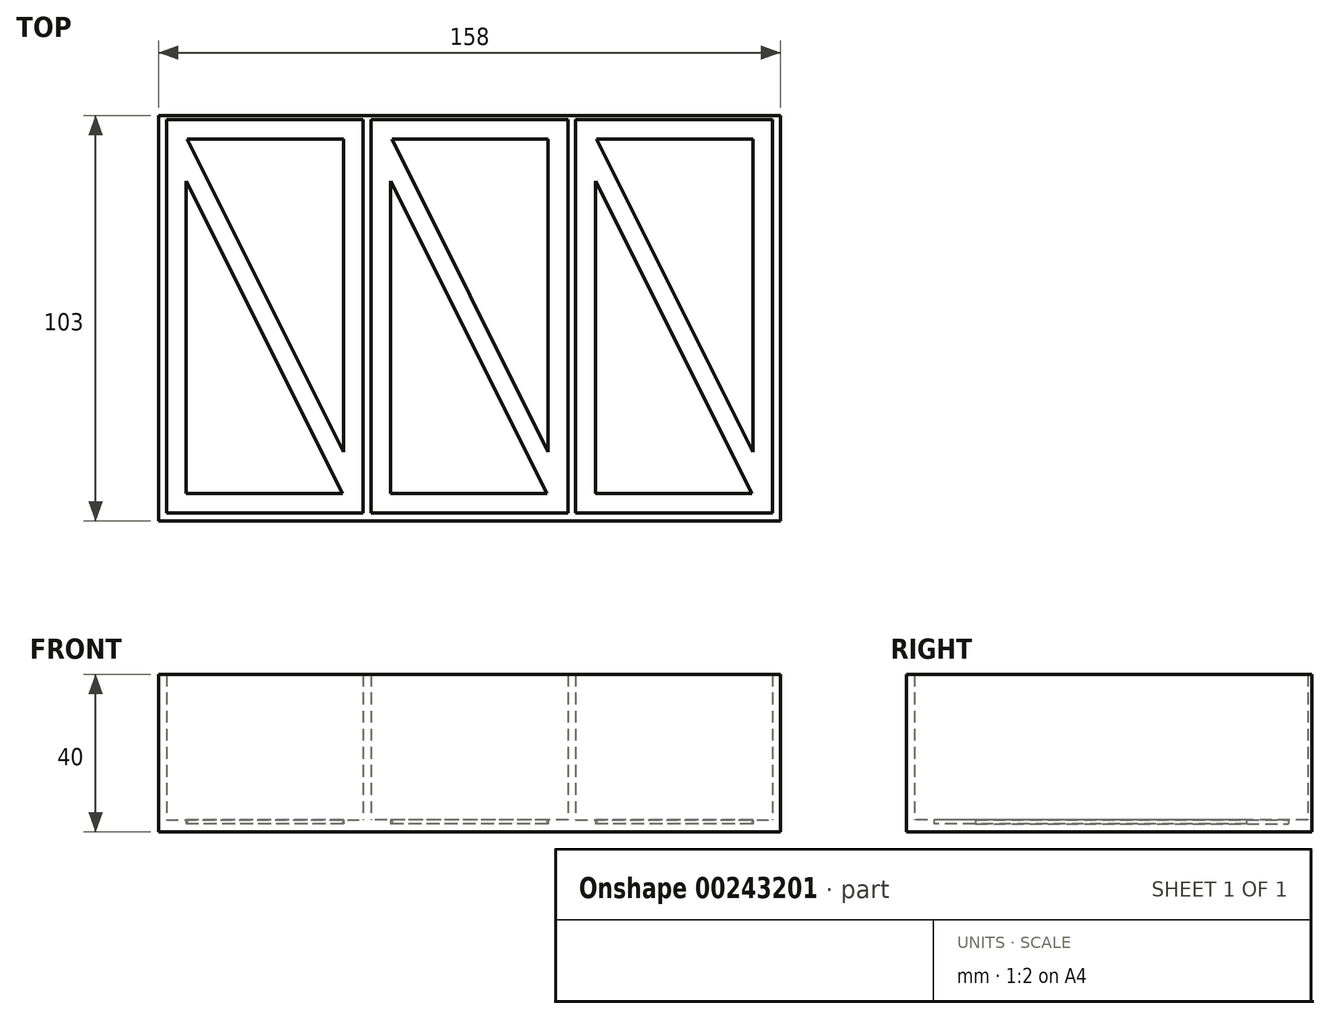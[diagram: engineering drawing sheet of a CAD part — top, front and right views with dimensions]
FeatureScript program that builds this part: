
annotation { "Feature Type Name" : "Feature", "Feature Type Description" : "" }
export const myFeature = defineFeature(function(context is Context, id is Id, definition is map)
    precondition{}
    {
        {
            var Q0;
            Q0=qCreatedBy(makeId("Top.planeOp"),FACE);
            var sketch = newSketch(context, id + "F0", { "sketchPlane" : qUnion([Q0])});
            skLineSegment(sketch, "E0.bottom", {"start": v(-25, 50) * mm, "end": v(25, 50) * mm});
            skLineSegment(sketch, "E0.top", {"start": v(-25, -50) * mm, "end": v(25, -50) * mm});
            skLineSegment(sketch, "E0.left", {"start": v(-25, 50) * mm, "end": v(-25, -50) * mm});
            skLineSegment(sketch, "E0.right", {"start": v(25, 50) * mm, "end": v(25, -50) * mm});
            skLineSegment(sketch, "E1", {"start": v(26, 57.33) * mm, "end": v(26, -203.87) * mm, "construction": true});
            skLineSegment(sketch, "E2.MirrorCS", {"start": v(25, 50) * mm, "end": v(25, 150) * mm});
            skLineSegment(sketch, "E3.MirrorCS", {"start": v(-25, 50) * mm, "end": v(-25, 150) * mm});
            skLineSegment(sketch, "E4.MirrorCS", {"start": v(77, -50) * mm, "end": v(27, -50) * mm});
            skLineSegment(sketch, "E5.MirrorCS", {"start": v(77, 50) * mm, "end": v(77, -50) * mm});
            skLineSegment(sketch, "E6.MirrorCS", {"start": v(27, 50) * mm, "end": v(27, -50) * mm});
            skLineSegment(sketch, "E7.MirrorCS", {"start": v(77, 50) * mm, "end": v(27, 50) * mm});
            skLineSegment(sketch, "E8", {"start": v(78, 65.82) * mm, "end": v(78, -195.37) * mm, "construction": true});
            skLineSegment(sketch, "E9.MirrorCS", {"start": v(79, -50) * mm, "end": v(129, -50) * mm});
            skLineSegment(sketch, "E10.MirrorCS", {"start": v(79, 50) * mm, "end": v(79, -50) * mm});
            skLineSegment(sketch, "E11.MirrorCS", {"start": v(79, 50) * mm, "end": v(129, 50) * mm});
            skLineSegment(sketch, "E12.MirrorCS", {"start": v(129, 50) * mm, "end": v(129, -50) * mm});
            skLineSegment(sketch, "E13.bottom", {"start": v(-27, 51) * mm, "end": v(131, 51) * mm});
            skLineSegment(sketch, "E13.top", {"start": v(-27, -52) * mm, "end": v(131, -52) * mm});
            skLineSegment(sketch, "E13.left", {"start": v(-27, 51) * mm, "end": v(-27, -52) * mm});
            skLineSegment(sketch, "E13.right", {"start": v(131, 51) * mm, "end": v(131, -52) * mm});
            skLineSegment(sketch, "E14", {"start": v(-25, 50) * mm, "end": v(25, -50) * mm, "construction": true});
            skLineSegment(sketch, "E15", {"start": v(-20, 34.4) * mm, "end": v(-20, -45) * mm});
            skLineSegment(sketch, "E16", {"start": v(-20, -45) * mm, "end": v(19.7, -45) * mm});
            skLineSegment(sketch, "E17", {"start": v(19.7, -45) * mm, "end": v(-20, 34.4) * mm});
            skLineSegment(sketch, "E18", {"start": v(-19.7, 45) * mm, "end": v(20, 45) * mm});
            skLineSegment(sketch, "E19", {"start": v(20, 45) * mm, "end": v(20, -34.4) * mm});
            skLineSegment(sketch, "E20", {"start": v(20, -34.4) * mm, "end": v(-19.7, 45) * mm});
            skLineSegment(sketch, "E21.1.0.0", {"start": v(32.3, 45) * mm, "end": v(72, 45) * mm});
            skLineSegment(sketch, "E21.1.0.1", {"start": v(72, 45) * mm, "end": v(72, -34.4) * mm});
            skLineSegment(sketch, "E21.1.0.2", {"start": v(72, -34.4) * mm, "end": v(32.3, 45) * mm});
            skLineSegment(sketch, "E21.1.0.3", {"start": v(71.7, -45) * mm, "end": v(32, 34.4) * mm});
            skLineSegment(sketch, "E21.1.0.4", {"start": v(32, 34.4) * mm, "end": v(32, -45) * mm});
            skLineSegment(sketch, "E21.1.0.5", {"start": v(32, -45) * mm, "end": v(71.7, -45) * mm});
            skLineSegment(sketch, "E21.2.0.0", {"start": v(84.3, 45) * mm, "end": v(124, 45) * mm});
            skLineSegment(sketch, "E21.2.0.1", {"start": v(124, 45) * mm, "end": v(124, -34.4) * mm});
            skLineSegment(sketch, "E21.2.0.2", {"start": v(124, -34.4) * mm, "end": v(84.3, 45) * mm});
            skLineSegment(sketch, "E21.2.0.3", {"start": v(123.7, -45) * mm, "end": v(84, 34.4) * mm});
            skLineSegment(sketch, "E21.2.0.4", {"start": v(84, 34.4) * mm, "end": v(84, -45) * mm});
            skLineSegment(sketch, "E21.2.0.5", {"start": v(84, -45) * mm, "end": v(123.7, -45) * mm});
            skLineSegment(sketch, "E21.direction1", {"start": v(-20, -45) * mm, "end": v(32, -45) * mm, "construction": true});
            skSolve(sketch);
        }
        {
            var Q0;
            Q0=makeQuery(id+"F0.imprint","IMPRINT",FACE,{"disambiguationData":[TD([[makeQuery(id+"F0.imprint","IMPRINT",EDGE,{"derivedFrom":sQuery(id+"F0.wireOp",EDGE,"E0.top")}),-1.0]])]});
            var Q1;
            {var subQ0=sQuery(id+"F0.wireOp",EDGE,"E0.bottom");Q1=makeQuery(id+"F0.imprint","IMPRINT",FACE,{"disambiguationData":[TD([[makeQuery(id+"F0.imprint","IMPRINT",EDGE,{"derivedFrom":subQ0}),1.0]])]});}
            extrude(context, id + "F1", {"entities" : qUnion([Q0, Q1]), "depth" : 40 * mm});
        }
        {
            var Q0;
            Q0=makeQuery(id+"F0.imprint","IMPRINT",FACE,{"disambiguationData":[TD([[makeQuery(id+"F0.imprint","IMPRINT",EDGE,{"derivedFrom":sQuery(id+"F0.wireOp",EDGE,"E0.bottom")}),-1.0]])]});
            var Q1;
            Q1=makeQuery(id+"F0.imprint","IMPRINT",FACE,{"disambiguationData":[TD([[makeQuery(id+"F0.imprint","IMPRINT",EDGE,{"derivedFrom":sQuery(id+"F0.wireOp",EDGE,"E4.MirrorCS")}),-1.0]])]});
            var Q2;
            Q2=makeQuery(id+"F0.imprint","IMPRINT",FACE,{"disambiguationData":[TD([[makeQuery(id+"F0.imprint","IMPRINT",EDGE,{"derivedFrom":sQuery(id+"F0.wireOp",EDGE,"E9.MirrorCS")}),1.0]])]});
            extrude(context, id + "F2", {"entities" : qUnion([Q0, Q1, Q2]), "operationType" : NewBodyOperationType.ADD, "depth" : 3 * mm});
        }
        {
            var Q0;
            Q0=makeQuery(id+"F0.imprint","IMPRINT",FACE,{"disambiguationData":[TD([[makeQuery(id+"F0.imprint","IMPRINT",EDGE,{"derivedFrom":sQuery(id+"F0.wireOp",EDGE,"E18")}),-1.0]])]});
            var Q1;
            Q1=makeQuery(id+"F0.imprint","IMPRINT",FACE,{"disambiguationData":[TD([[makeQuery(id+"F0.imprint","IMPRINT",EDGE,{"derivedFrom":sQuery(id+"F0.wireOp",EDGE,"E15")}),1.0]])]});
            var Q2;
            Q2=makeQuery(id+"F0.imprint","IMPRINT",FACE,{"disambiguationData":[TD([[makeQuery(id+"F0.imprint","IMPRINT",EDGE,{"derivedFrom":sQuery(id+"F0.wireOp",EDGE,"E21.1.0.3")}),1.0]])]});
            var Q3;
            Q3=makeQuery(id+"F0.imprint","IMPRINT",FACE,{"disambiguationData":[TD([[makeQuery(id+"F0.imprint","IMPRINT",EDGE,{"derivedFrom":sQuery(id+"F0.wireOp",EDGE,"E21.1.0.0")}),-1.0]])]});
            var Q4;
            Q4=makeQuery(id+"F0.imprint","IMPRINT",FACE,{"disambiguationData":[TD([[makeQuery(id+"F0.imprint","IMPRINT",EDGE,{"derivedFrom":sQuery(id+"F0.wireOp",EDGE,"E21.2.0.0")}),-1.0]])]});
            var Q5;
            Q5=makeQuery(id+"F0.imprint","IMPRINT",FACE,{"disambiguationData":[TD([[makeQuery(id+"F0.imprint","IMPRINT",EDGE,{"derivedFrom":sQuery(id+"F0.wireOp",EDGE,"E21.2.0.3")}),1.0]])]});
            extrude(context, id + "F3", {"entities" : qUnion([Q0, Q1, Q2, Q3, Q4, Q5]), "operationType" : NewBodyOperationType.ADD, "depth" : 2 * mm});
        }
    });
